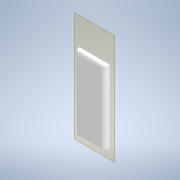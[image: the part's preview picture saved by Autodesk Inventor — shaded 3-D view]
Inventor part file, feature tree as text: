
AUTODESK INVENTOR PART (.ipt)
format: ipt  version: 2021 (Build 250183000, 183)  size: 115,200 bytes
history: native  units: mm
features: other x5, extrude x1, fillet x1, sketch x1, reference x1
ambient origin geometry x8: Origin, YZ Plane, XZ Plane, XY Plane, X Axis, Y Axis, Z Axis, Center Point
bodies: Body1 (feature_tree)
feature tree (9):
  other  "Bryła1"
  other  "Płaszczyzna konstrukcyjna1"
  extrude  "Wyciągnięcie proste1"  Depth=1.0mm
  fillet  "Zaokrąglenie1"  Radius=1.5mm
  sketch  "Szkic1"
  reference  "Odniesienie1"
  parser-record x1  (decoder bookkeeping rows leaked as tree rows — omitted from the tree; the rows remain in map.json)
  other  "model tensometru.iam"
  other  "tensometr:1"
note: 1 file-system path scrubbed to <path> (originals preserved in map.json)
